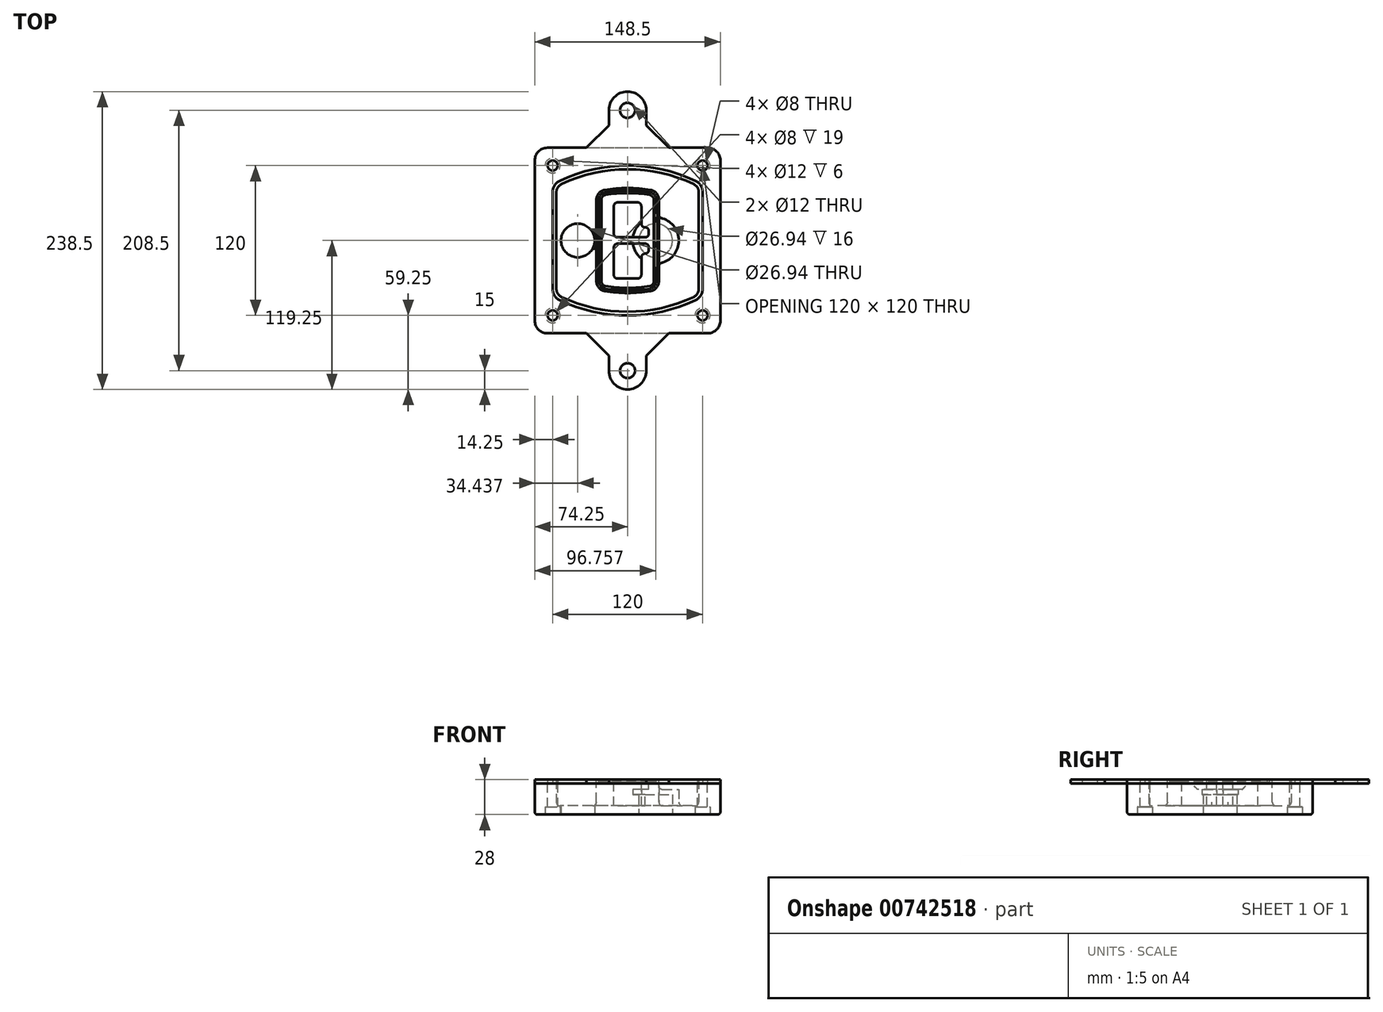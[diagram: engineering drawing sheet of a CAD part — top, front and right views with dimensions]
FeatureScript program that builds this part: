
annotation { "Feature Type Name" : "Feature", "Feature Type Description" : "" }
export const myFeature = defineFeature(function(context is Context, id is Id, definition is map)
    precondition{}
    {
        {
            var Q0;
            Q0=qCreatedBy(makeId("Top.planeOp"),FACE);
            var sketch = newSketch(context, id + "F0", { "sketchPlane" : qUnion([Q0])});
            skPoint(sketch, "E0.rect.middle", {"position": v(0, 0) * mm});
            skLineSegment(sketch, "E1.bottom", {"start": v(-64.25, -74.25) * mm, "end": v(64.25, -74.25) * mm});
            skLineSegment(sketch, "E1.top", {"start": v(-64.25, 74.25) * mm, "end": v(64.25, 74.25) * mm});
            skLineSegment(sketch, "E1.left", {"start": v(-74.25, -64.25) * mm, "end": v(-74.25, 64.25) * mm});
            skLineSegment(sketch, "E1.right", {"start": v(74.25, -64.25) * mm, "end": v(74.25, 64.25) * mm});
            skLineSegment(sketch, "E2", {"start": v(-74.25, 74.25) * mm, "end": v(74.25, -74.25) * mm, "construction": true});
            skLineSegment(sketch, "E3", {"start": v(74.25, 74.25) * mm, "end": v(-74.25, -74.25) * mm, "construction": true});
            skCircle(sketch, "E4", {"center": v(-60, 60) * mm, "radius": 4 * mm});
            skCircle(sketch, "E5", {"center": v(60, 60) * mm, "radius": 4 * mm});
            skCircle(sketch, "E6", {"center": v(60, -60) * mm, "radius": 4 * mm});
            skCircle(sketch, "E7", {"center": v(-60, -60) * mm, "radius": 4 * mm});
            skLineSegment(sketch, "E8", {"start": v(-60, 60) * mm, "end": v(60, 60) * mm, "construction": true});
            skLineSegment(sketch, "E9", {"start": v(60, 60) * mm, "end": v(60, -60) * mm, "construction": true});
            skLineSegment(sketch, "E10", {"start": v(60, -60) * mm, "end": v(-60, -60) * mm, "construction": true});
            skLineSegment(sketch, "E11", {"start": v(-60, -60) * mm, "end": v(-60, 60) * mm, "construction": true});
            skLineSegment(sketch, "E12", {"start": v(-60, 38.83) * mm, "end": v(-60, -38.83) * mm});
            skLineSegment(sketch, "E13", {"start": v(60, 38.83) * mm, "end": v(60, -38.83) * mm});
            skArc(sketch, "E14", {"start": v(54.26, 47.88) * mm, "mid": v(0, 60) * mm, "end": v(-54.26, 47.88) * mm});
            skArc(sketch, "E15", {"start": v(-54.26, -47.88) * mm, "mid": v(0, -60) * mm, "end": v(54.26, -47.88) * mm});
            skLineSegment(sketch, "E16", {"start": v(-60, 0) * mm, "end": v(60, 0) * mm, "construction": true});
            skPoint(sketch, "E17.visualSharp", {"position": v(-60, -45) * mm});
            skArc(sketch, "E17.filletArc", {"start": v(-60, -38.83) * mm, "mid": v(-58.44, -44.2) * mm, "end": v(-54.26, -47.88) * mm});
            skPoint(sketch, "E18.visualSharp", {"position": v(-60, 45) * mm});
            skArc(sketch, "E18.filletArc", {"start": v(-54.26, 47.88) * mm, "mid": v(-58.44, 44.2) * mm, "end": v(-60, 38.83) * mm});
            skPoint(sketch, "E19.visualSharp", {"position": v(60, 45) * mm});
            skArc(sketch, "E19.filletArc", {"start": v(60, 38.83) * mm, "mid": v(58.44, 44.2) * mm, "end": v(54.26, 47.88) * mm});
            skPoint(sketch, "E20.visualSharp", {"position": v(60, -45) * mm});
            skArc(sketch, "E20.filletArc", {"start": v(54.26, -47.88) * mm, "mid": v(58.44, -44.2) * mm, "end": v(60, -38.83) * mm});
            skPoint(sketch, "E21.visualSharp", {"position": v(-74.25, 74.25) * mm});
            skArc(sketch, "E21.filletArc", {"start": v(-64.25, 74.25) * mm, "mid": v(-71.32, 71.32) * mm, "end": v(-74.25, 64.25) * mm});
            skPoint(sketch, "E22.visualSharp", {"position": v(74.25, 74.25) * mm});
            skArc(sketch, "E22.filletArc", {"start": v(74.25, 64.25) * mm, "mid": v(71.32, 71.32) * mm, "end": v(64.25, 74.25) * mm});
            skPoint(sketch, "E23.visualSharp", {"position": v(74.25, -74.25) * mm});
            skArc(sketch, "E23.filletArc", {"start": v(64.25, -74.25) * mm, "mid": v(71.32, -71.32) * mm, "end": v(74.25, -64.25) * mm});
            skPoint(sketch, "E24.visualSharp", {"position": v(-74.25, -74.25) * mm});
            skArc(sketch, "E24.filletArc", {"start": v(-74.25, -64.25) * mm, "mid": v(-71.32, -71.32) * mm, "end": v(-64.25, -74.25) * mm});
            skArc(sketch, "E25.0", {"start": v(57, 38.83) * mm, "mid": v(55.9, 42.58) * mm, "end": v(52.98, 45.17) * mm});
            skLineSegment(sketch, "E25.1", {"start": v(57, 38.83) * mm, "end": v(57, -38.83) * mm});
            skArc(sketch, "E25.2", {"start": v(52.98, -45.17) * mm, "mid": v(55.9, -42.58) * mm, "end": v(57, -38.83) * mm});
            skArc(sketch, "E25.3", {"start": v(-52.98, -45.17) * mm, "mid": v(0, -57) * mm, "end": v(52.98, -45.17) * mm});
            skArc(sketch, "E25.4", {"start": v(-57, -38.83) * mm, "mid": v(-55.9, -42.58) * mm, "end": v(-52.98, -45.17) * mm});
            skArc(sketch, "E25.5", {"start": v(52.98, 45.17) * mm, "mid": v(0, 57) * mm, "end": v(-52.98, 45.17) * mm});
            skLineSegment(sketch, "E25.6", {"start": v(-57, 38.83) * mm, "end": v(-57, -38.83) * mm});
            skArc(sketch, "E25.7", {"start": v(-52.98, 45.17) * mm, "mid": v(-55.9, 42.58) * mm, "end": v(-57, 38.83) * mm});
            skArc(sketch, "E26.0", {"start": v(-55.96, 51.5) * mm, "mid": v(-61.82, 46.33) * mm, "end": v(-64, 38.83) * mm});
            skArc(sketch, "E26.1", {"start": v(55.96, 51.5) * mm, "mid": v(0, 64) * mm, "end": v(-55.96, 51.5) * mm});
            skArc(sketch, "E26.2", {"start": v(64, 38.83) * mm, "mid": v(61.82, 46.33) * mm, "end": v(55.96, 51.5) * mm});
            skLineSegment(sketch, "E26.3", {"start": v(64, 38.83) * mm, "end": v(64, -38.83) * mm});
            skArc(sketch, "E26.4", {"start": v(55.96, -51.5) * mm, "mid": v(61.82, -46.33) * mm, "end": v(64, -38.83) * mm});
            skLineSegment(sketch, "E26.5", {"start": v(-64, 38.83) * mm, "end": v(-64, -38.83) * mm});
            skArc(sketch, "E26.6", {"start": v(-55.96, -51.5) * mm, "mid": v(0, -64) * mm, "end": v(55.96, -51.5) * mm});
            skArc(sketch, "E26.7", {"start": v(-64, -38.83) * mm, "mid": v(-61.82, -46.33) * mm, "end": v(-55.96, -51.5) * mm});
            skSolve(sketch);
        }
        {
            var Q0;
            Q0=makeQuery(id+"F0.imprint","IMPRINT",FACE,{"disambiguationData":[TD([[makeQuery(id+"F0.imprint","IMPRINT",EDGE,{"derivedFrom":sQuery(id+"F0.wireOp",EDGE,"E1.bottom")}),1.0]])]});
            var Q1;
            Q1=makeQuery(id+"F0.imprint","IMPRINT",FACE,{"disambiguationData":[TD([[makeQuery(id+"F0.imprint","IMPRINT",EDGE,{"derivedFrom":sQuery(id+"F0.wireOp",EDGE,"E12")}),1.0]])]});
            var Q2;
            Q2=makeQuery(id+"F0.imprint","IMPRINT",FACE,{"disambiguationData":[TD([[makeQuery(id+"F0.imprint","IMPRINT",EDGE,{"derivedFrom":sQuery(id+"F0.wireOp",EDGE,"E25.0")}),1.0]])]});
            var Q3;
            Q3=makeQuery(id+"F0.imprint","IMPRINT",FACE,{"disambiguationData":[TD([[makeQuery(id+"F0.imprint","IMPRINT",EDGE,{"derivedFrom":sQuery(id+"F0.wireOp",EDGE,"E12")}),-1.0]])]});
            extrude(context, id + "F1", {"entities" : qUnion([Q0, Q1, Q2, Q3]), "oppositeDirection" : true, "depth" : 25 * mm});
        }
        {
            var Q0;
            Q0=makeQuery(id+"F0.imprint","IMPRINT",FACE,{"disambiguationData":[TD([[makeQuery(id+"F0.imprint","IMPRINT",EDGE,{"derivedFrom":sQuery(id+"F0.wireOp",EDGE,"E12")}),1.0]])]});
            extrude(context, id + "F2", {"entities" : qUnion([Q0]), "operationType" : NewBodyOperationType.ADD, "depth" : 3 * mm});
        }
        {
            var Q0;
            Q0=makeQuery(id+"F0.imprint","IMPRINT",FACE,{"disambiguationData":[TD([[makeQuery(id+"F0.imprint","IMPRINT",EDGE,{"derivedFrom":sQuery(id+"F0.wireOp",EDGE,"E25.0")}),1.0]])]});
            extrude(context, id + "F3", {"entities" : qUnion([Q0]), "operationType" : NewBodyOperationType.REMOVE, "oppositeDirection" : true, "depth" : 18 * mm});
        }
        {
            var Q0;
            Q0=makeQuery(id+"F2.opExtrude","CAP_FACE",FACE,{"disambiguationData":[OSD([sQuery(id+"F0.wireOp",EDGE,"E12"),sQuery(id+"F0.wireOp",EDGE,"E13"),sQuery(id+"F0.wireOp",EDGE,"E14"),sQuery(id+"F0.wireOp",EDGE,"E15"),sQuery(id+"F0.wireOp",EDGE,"E17.filletArc"),sQuery(id+"F0.wireOp",EDGE,"E18.filletArc"),sQuery(id+"F0.wireOp",EDGE,"E19.filletArc"),sQuery(id+"F0.wireOp",EDGE,"E20.filletArc"),sQuery(id+"F0.wireOp",EDGE,"E25.0"),sQuery(id+"F0.wireOp",EDGE,"E25.1"),sQuery(id+"F0.wireOp",EDGE,"E25.2"),sQuery(id+"F0.wireOp",EDGE,"E25.3"),sQuery(id+"F0.wireOp",EDGE,"E25.4"),sQuery(id+"F0.wireOp",EDGE,"E25.5"),sQuery(id+"F0.wireOp",EDGE,"E25.6"),sQuery(id+"F0.wireOp",EDGE,"E25.7")])],"isStart":false});
            var sketch = newSketch(context, id + "F4", { "sketchPlane" : qUnion([Q0])});
            skArc(sketch, "E27.0", {"start": v(-18.34, -40.45) * mm, "mid": v(0, -42) * mm, "end": v(18.34, -40.45) * mm});
            skArc(sketch, "E28.0", {"start": v(18.34, 40.45) * mm, "mid": v(0, 42) * mm, "end": v(-18.34, 40.45) * mm});
            skLineSegment(sketch, "E29", {"start": v(-25, 32.57) * mm, "end": v(-25, -32.57) * mm});
            skLineSegment(sketch, "E30", {"start": v(25, 32.57) * mm, "end": v(25, -32.57) * mm});
            skLineSegment(sketch, "E31", {"start": v(-25, 39.1) * mm, "end": v(25, 39.1) * mm, "construction": true});
            skLineSegment(sketch, "E32", {"start": v(-25, -39.1) * mm, "end": v(25, -39.1) * mm, "construction": true});
            skPoint(sketch, "E33.visualSharp", {"position": v(-25, 39.1) * mm});
            skArc(sketch, "E33.filletArc", {"start": v(-18.34, 40.45) * mm, "mid": v(-23.11, 37.73) * mm, "end": v(-25, 32.57) * mm});
            skPoint(sketch, "E34.visualSharp", {"position": v(25, 39.1) * mm});
            skArc(sketch, "E34.filletArc", {"start": v(25, 32.57) * mm, "mid": v(23.11, 37.73) * mm, "end": v(18.34, 40.45) * mm});
            skPoint(sketch, "E35.visualSharp", {"position": v(25, -39.1) * mm});
            skArc(sketch, "E35.filletArc", {"start": v(18.34, -40.45) * mm, "mid": v(23.11, -37.73) * mm, "end": v(25, -32.57) * mm});
            skPoint(sketch, "E36.visualSharp", {"position": v(-25, -39.1) * mm});
            skArc(sketch, "E36.filletArc", {"start": v(-25, -32.57) * mm, "mid": v(-23.11, -37.73) * mm, "end": v(-18.34, -40.45) * mm});
            skArc(sketch, "E37.0", {"start": v(52.98, 45.17) * mm, "mid": v(0, 57) * mm, "end": v(-52.98, 45.17) * mm});
            skArc(sketch, "E37.1", {"start": v(-52.98, 45.17) * mm, "mid": v(-55.9, 42.58) * mm, "end": v(-57, 38.83) * mm});
            skLineSegment(sketch, "E37.2", {"start": v(-57, 38.83) * mm, "end": v(-57, -38.83) * mm});
            skArc(sketch, "E37.3", {"start": v(-57, -38.83) * mm, "mid": v(-55.9, -42.58) * mm, "end": v(-52.98, -45.17) * mm});
            skArc(sketch, "E37.4", {"start": v(-52.98, -45.17) * mm, "mid": v(0, -57) * mm, "end": v(52.98, -45.17) * mm});
            skArc(sketch, "E37.5", {"start": v(52.98, -45.17) * mm, "mid": v(55.9, -42.58) * mm, "end": v(57, -38.83) * mm});
            skLineSegment(sketch, "E37.6", {"start": v(57, 38.83) * mm, "end": v(57, -38.83) * mm});
            skArc(sketch, "E37.7", {"start": v(57, 38.83) * mm, "mid": v(55.9, 42.58) * mm, "end": v(52.98, 45.17) * mm});
            skLineSegment(sketch, "E38.0", {"start": v(23, 32.57) * mm, "end": v(23, -32.57) * mm});
            skArc(sketch, "E38.1", {"start": v(18, -38.48) * mm, "mid": v(21.58, -36.44) * mm, "end": v(23, -32.57) * mm});
            skArc(sketch, "E38.2", {"start": v(-18, -38.48) * mm, "mid": v(0, -40) * mm, "end": v(18, -38.48) * mm});
            skArc(sketch, "E38.3", {"start": v(-23, -32.57) * mm, "mid": v(-21.58, -36.44) * mm, "end": v(-18, -38.48) * mm});
            skLineSegment(sketch, "E38.4", {"start": v(-23, 32.57) * mm, "end": v(-23, -32.57) * mm});
            skArc(sketch, "E38.5", {"start": v(23, 32.57) * mm, "mid": v(21.58, 36.44) * mm, "end": v(18, 38.48) * mm});
            skArc(sketch, "E38.6", {"start": v(-18, 38.48) * mm, "mid": v(-21.58, 36.44) * mm, "end": v(-23, 32.57) * mm});
            skArc(sketch, "E38.7", {"start": v(18, 38.48) * mm, "mid": v(0, 40) * mm, "end": v(-18, 38.48) * mm});
            skArc(sketch, "E39.0", {"start": v(21, 32.57) * mm, "mid": v(20.06, 35.15) * mm, "end": v(17.67, 36.5) * mm});
            skLineSegment(sketch, "E39.1", {"start": v(21, 32.57) * mm, "end": v(21, -32.57) * mm});
            skArc(sketch, "E39.2", {"start": v(17.67, -36.5) * mm, "mid": v(20.06, -35.15) * mm, "end": v(21, -32.57) * mm});
            skArc(sketch, "E39.3", {"start": v(-17.67, -36.5) * mm, "mid": v(0, -38) * mm, "end": v(17.67, -36.5) * mm});
            skArc(sketch, "E39.4", {"start": v(-21, -32.57) * mm, "mid": v(-20.06, -35.15) * mm, "end": v(-17.67, -36.5) * mm});
            skArc(sketch, "E39.5", {"start": v(17.67, 36.5) * mm, "mid": v(0, 38) * mm, "end": v(-17.67, 36.5) * mm});
            skLineSegment(sketch, "E39.6", {"start": v(-21, 32.57) * mm, "end": v(-21, -32.57) * mm});
            skArc(sketch, "E39.7", {"start": v(-17.67, 36.5) * mm, "mid": v(-20.06, 35.15) * mm, "end": v(-21, 32.57) * mm});
            skLineSegment(sketch, "E40", {"start": v(-25, 0) * mm, "end": v(25, 0) * mm, "construction": true});
            skLineSegment(sketch, "E41", {"start": v(-11, 5.5) * mm, "end": v(-11, 27.5) * mm});
            skLineSegment(sketch, "E42", {"start": v(-8, 30.5) * mm, "end": v(8, 30.5) * mm});
            skLineSegment(sketch, "E43", {"start": v(11, 27.5) * mm, "end": v(11, 13.5) * mm});
            skLineSegment(sketch, "E44", {"start": v(14, 10.5) * mm, "end": v(14, 10.5) * mm});
            skLineSegment(sketch, "E45", {"start": v(17, 7.5) * mm, "end": v(17, 5.5) * mm});
            skLineSegment(sketch, "E46", {"start": v(14, 2.5) * mm, "end": v(-8, 2.5) * mm});
            skPoint(sketch, "E47.visualSharp", {"position": v(-11, 30.5) * mm});
            skArc(sketch, "E47.filletArc", {"start": v(-8, 30.5) * mm, "mid": v(-10.12, 29.62) * mm, "end": v(-11, 27.5) * mm});
            skPoint(sketch, "E48.visualSharp", {"position": v(11, 30.5) * mm});
            skArc(sketch, "E48.filletArc", {"start": v(11, 27.5) * mm, "mid": v(10.12, 29.62) * mm, "end": v(8, 30.5) * mm});
            skPoint(sketch, "E49.visualSharp", {"position": v(11, 10.5) * mm});
            skArc(sketch, "E49.filletArc", {"start": v(11, 13.5) * mm, "mid": v(11.88, 11.38) * mm, "end": v(14, 10.5) * mm});
            skPoint(sketch, "E50.visualSharp", {"position": v(17, 10.5) * mm});
            skArc(sketch, "E50.filletArc", {"start": v(17, 7.5) * mm, "mid": v(16.12, 9.62) * mm, "end": v(14, 10.5) * mm});
            skPoint(sketch, "E51.visualSharp", {"position": v(17, 2.5) * mm});
            skArc(sketch, "E51.filletArc", {"start": v(14, 2.5) * mm, "mid": v(16.12, 3.38) * mm, "end": v(17, 5.5) * mm});
            skPoint(sketch, "E52.visualSharp", {"position": v(-11, 2.5) * mm});
            skArc(sketch, "E52.filletArc", {"start": v(-11, 5.5) * mm, "mid": v(-10.12, 3.38) * mm, "end": v(-8, 2.5) * mm});
            skLineSegment(sketch, "E53.0.MirrorCS", {"start": v(14, -2.5) * mm, "end": v(-8, -2.5) * mm});
            skArc(sketch, "E54.0.MirrorCS", {"start": v(-11, -5.5) * mm, "mid": v(-10.12, -3.38) * mm, "end": v(-8, -2.5) * mm});
            skLineSegment(sketch, "E55.0.MirrorCS", {"start": v(-11, -5.5) * mm, "end": v(-11, -27.5) * mm});
            skArc(sketch, "E56.0.MirrorCS", {"start": v(-8, -30.5) * mm, "mid": v(-10.12, -29.62) * mm, "end": v(-11, -27.5) * mm});
            skLineSegment(sketch, "E57.0.MirrorCS", {"start": v(-8, -30.5) * mm, "end": v(8, -30.5) * mm});
            skArc(sketch, "E58.0.MirrorCS", {"start": v(11, -27.5) * mm, "mid": v(10.12, -29.62) * mm, "end": v(8, -30.5) * mm});
            skLineSegment(sketch, "E59.0.MirrorCS", {"start": v(11, -27.5) * mm, "end": v(11, -13.5) * mm});
            skArc(sketch, "E60.0.MirrorCS", {"start": v(11, -13.5) * mm, "mid": v(11.88, -11.38) * mm, "end": v(14, -10.5) * mm});
            skArc(sketch, "E61.0.MirrorCS", {"start": v(17, -7.5) * mm, "mid": v(16.12, -9.62) * mm, "end": v(14, -10.5) * mm});
            skLineSegment(sketch, "E62.0.MirrorCS", {"start": v(17, -7.5) * mm, "end": v(17, -5.5) * mm});
            skArc(sketch, "E63.0.MirrorCS", {"start": v(14, -2.5) * mm, "mid": v(16.12, -3.38) * mm, "end": v(17, -5.5) * mm});
            skSolve(sketch);
        }
        {
            var Q0;
            Q0=makeQuery(id+"F4.imprint","IMPRINT",FACE,{"disambiguationData":[TD([[makeQuery(id+"F4.imprint","IMPRINT",EDGE,{"derivedFrom":sQuery(id+"F4.wireOp",EDGE,"E27.0")}),1.0]])]});
            var Q1;
            Q1=makeQuery(id+"F4.imprint","IMPRINT",FACE,{"disambiguationData":[TD([[makeQuery(id+"F4.imprint","IMPRINT",EDGE,{"derivedFrom":sQuery(id+"F4.wireOp",EDGE,"E38.0")}),-1.0]])]});
            var Q2;
            Q2=makeQuery(id+"F4.imprint","IMPRINT",FACE,{"disambiguationData":[TD([[makeQuery(id+"F4.imprint","IMPRINT",EDGE,{"derivedFrom":sQuery(id+"F4.wireOp",EDGE,"E39.0")}),1.0]])]});
            extrude(context, id + "F5", {"entities" : qUnion([Q0, Q1, Q2]), "operationType" : NewBodyOperationType.ADD, "endBound" : BoundingType.UP_TO_NEXT, "oppositeDirection" : true, "depth" : 25 * mm});
        }
        {
            var Q0;
            Q0=makeQuery(id+"F4.imprint","IMPRINT",FACE,{"disambiguationData":[TD([[makeQuery(id+"F4.imprint","IMPRINT",EDGE,{"derivedFrom":sQuery(id+"F4.wireOp",EDGE,"E38.0")}),-1.0]])]});
            extrude(context, id + "F6", {"entities" : qUnion([Q0]), "operationType" : NewBodyOperationType.REMOVE, "oppositeDirection" : true, "depth" : 2 * mm});
        }
        {
            var Q0;
            Q0=makeQuery(id+"F1.opExtrude","CAP_FACE",FACE,{"disambiguationData":[OSD([sQuery(id+"F0.wireOp",EDGE,"E1.bottom"),sQuery(id+"F0.wireOp",EDGE,"E1.top"),sQuery(id+"F0.wireOp",EDGE,"E1.left"),sQuery(id+"F0.wireOp",EDGE,"E1.right"),sQuery(id+"F0.wireOp",EDGE,"E4"),sQuery(id+"F0.wireOp",EDGE,"E5"),sQuery(id+"F0.wireOp",EDGE,"E6"),sQuery(id+"F0.wireOp",EDGE,"E7"),sQuery(id+"F0.wireOp",EDGE,"E21.filletArc"),sQuery(id+"F0.wireOp",EDGE,"E22.filletArc"),sQuery(id+"F0.wireOp",EDGE,"E23.filletArc"),sQuery(id+"F0.wireOp",EDGE,"E24.filletArc")])],"isStart":false});
            var sketch = newSketch(context, id + "F7", { "sketchPlane" : qUnion([Q0])});
            skCircle(sketch, "E64", {"center": v(22.5, 0) * mm, "radius": 13.47 * mm});
            skCircle(sketch, "E65", {"center": v(-39.81, 0) * mm, "radius": 13.47 * mm});
            skLineSegment(sketch, "E66", {"start": v(74.25, 0) * mm, "end": v(-74.25, 0) * mm});
            skCircle(sketch, "E67", {"center": v(22.5, 0) * mm, "radius": 18.47 * mm});
            skCircle(sketch, "E68", {"center": v(60, -60) * mm, "radius": 6 * mm});
            skCircle(sketch, "E69", {"center": v(-60, -60) * mm, "radius": 6 * mm});
            skCircle(sketch, "E70", {"center": v(-60, 60) * mm, "radius": 6 * mm});
            skCircle(sketch, "E71", {"center": v(60, 60) * mm, "radius": 6 * mm});
            skSolve(sketch);
        }
        {
            var Q0;
            {var subQ1=sQuery(id+"F7.wireOp",EDGE,"E66");var subQ4=sQuery(id+"F7.wireOp",EDGE,"E64");var subQ6=makeQuery(id+"F7.imprint","INTERSECT",VERTEX,{"disambiguationData":[OD(0.0)],"derivedFrom":[subQ4,subQ1]});Q0=makeQuery(id+"F7.imprint","IMPRINT",FACE,{"disambiguationData":[TD([[makeQuery(id+"F7.imprint","IMPRINT",EDGE,{"disambiguationData":[TD([[subQ6,-1.0]])],"derivedFrom":subQ4}),-1.0]])]});}
            var Q1;
            {var subQ0=sQuery(id+"F7.wireOp",EDGE,"E66");var subQ1=sQuery(id+"F7.wireOp",EDGE,"E64");var subQ3=makeQuery(id+"F7.imprint","INTERSECT",VERTEX,{"disambiguationData":[OD(0.0)],"derivedFrom":[subQ1,subQ0]});Q1=makeQuery(id+"F7.imprint","IMPRINT",FACE,{"disambiguationData":[TD([[makeQuery(id+"F7.imprint","IMPRINT",EDGE,{"disambiguationData":[TD([[subQ3,-1.0]])],"derivedFrom":subQ1}),1.0]])]});}
            var Q2;
            {var subQ0=sQuery(id+"F7.wireOp",EDGE,"E66");var subQ1=sQuery(id+"F7.wireOp",EDGE,"E64");var subQ3=makeQuery(id+"F7.imprint","INTERSECT",VERTEX,{"disambiguationData":[OD(0.0)],"derivedFrom":[subQ1,subQ0]});Q2=makeQuery(id+"F7.imprint","IMPRINT",FACE,{"disambiguationData":[TD([[makeQuery(id+"F7.imprint","IMPRINT",EDGE,{"disambiguationData":[TD([[subQ3,1.0]])],"derivedFrom":subQ1}),1.0]])]});}
            var Q3;
            {var subQ1=sQuery(id+"F7.wireOp",EDGE,"E66");var subQ4=sQuery(id+"F7.wireOp",EDGE,"E64");var subQ6=makeQuery(id+"F7.imprint","INTERSECT",VERTEX,{"disambiguationData":[OD(0.0)],"derivedFrom":[subQ4,subQ1]});Q3=makeQuery(id+"F7.imprint","IMPRINT",FACE,{"disambiguationData":[TD([[makeQuery(id+"F7.imprint","IMPRINT",EDGE,{"disambiguationData":[TD([[subQ6,1.0]])],"derivedFrom":subQ4}),-1.0]])]});}
            extrude(context, id + "F8", {"entities" : qUnion([Q0, Q1, Q2, Q3]), "operationType" : NewBodyOperationType.ADD, "oppositeDirection" : true, "depth" : 20 * mm});
        }
        {
            var Q0;
            {var subQ0=sQuery(id+"F7.wireOp",EDGE,"E66");var subQ1=sQuery(id+"F7.wireOp",EDGE,"E64");var subQ3=makeQuery(id+"F7.imprint","INTERSECT",VERTEX,{"disambiguationData":[OD(0.0)],"derivedFrom":[subQ1,subQ0]});Q0=makeQuery(id+"F7.imprint","IMPRINT",FACE,{"disambiguationData":[TD([[makeQuery(id+"F7.imprint","IMPRINT",EDGE,{"disambiguationData":[TD([[subQ3,-1.0]])],"derivedFrom":subQ1}),1.0]])]});}
            var Q1;
            {var subQ0=sQuery(id+"F7.wireOp",EDGE,"E66");var subQ1=sQuery(id+"F7.wireOp",EDGE,"E64");var subQ3=makeQuery(id+"F7.imprint","INTERSECT",VERTEX,{"disambiguationData":[OD(0.0)],"derivedFrom":[subQ1,subQ0]});Q1=makeQuery(id+"F7.imprint","IMPRINT",FACE,{"disambiguationData":[TD([[makeQuery(id+"F7.imprint","IMPRINT",EDGE,{"disambiguationData":[TD([[subQ3,1.0]])],"derivedFrom":subQ1}),1.0]])]});}
            extrude(context, id + "F9", {"entities" : qUnion([Q0, Q1]), "operationType" : NewBodyOperationType.REMOVE, "oppositeDirection" : true, "depth" : 16 * mm});
        }
        {
            var Q0;
            {var subQ0=sQuery(id+"F7.wireOp",EDGE,"E66");var subQ1=sQuery(id+"F7.wireOp",EDGE,"E65");var subQ3=makeQuery(id+"F7.imprint","INTERSECT",VERTEX,{"disambiguationData":[OD(0.0)],"derivedFrom":[subQ1,subQ0]});Q0=makeQuery(id+"F7.imprint","IMPRINT",FACE,{"disambiguationData":[TD([[makeQuery(id+"F7.imprint","IMPRINT",EDGE,{"disambiguationData":[TD([[subQ3,-1.0]])],"derivedFrom":subQ1}),1.0]])]});}
            var Q1;
            {var subQ0=sQuery(id+"F7.wireOp",EDGE,"E66");var subQ1=sQuery(id+"F7.wireOp",EDGE,"E65");var subQ3=makeQuery(id+"F7.imprint","INTERSECT",VERTEX,{"disambiguationData":[OD(0.0)],"derivedFrom":[subQ1,subQ0]});Q1=makeQuery(id+"F7.imprint","IMPRINT",FACE,{"disambiguationData":[TD([[makeQuery(id+"F7.imprint","IMPRINT",EDGE,{"disambiguationData":[TD([[subQ3,1.0]])],"derivedFrom":subQ1}),1.0]])]});}
            extrude(context, id + "F10", {"entities" : qUnion([Q0, Q1]), "operationType" : NewBodyOperationType.REMOVE, "oppositeDirection" : true, "depth" : 25 * mm});
        }
        {
            var Q0;
            Q0=makeQuery(id+"F7.imprint","IMPRINT",FACE,{"disambiguationData":[TD([[makeQuery(id+"F7.imprint","IMPRINT",EDGE,{"derivedFrom":sQuery(id+"F7.wireOp",EDGE,"E68")}),1.0]])]});
            var Q1;
            Q1=makeQuery(id+"F7.imprint","IMPRINT",FACE,{"disambiguationData":[TD([[makeQuery(id+"F7.imprint","IMPRINT",EDGE,{"derivedFrom":makeQuery(id+"F1.opExtrude","CAP_EDGE",EDGE,{"disambiguationData":[OSD([sQuery(id+"F0.wireOp",EDGE,"E5")])],"isStart":false})}),-1.0]])]});
            var Q2;
            Q2=makeQuery(id+"F7.imprint","IMPRINT",FACE,{"disambiguationData":[TD([[makeQuery(id+"F7.imprint","IMPRINT",EDGE,{"derivedFrom":sQuery(id+"F7.wireOp",EDGE,"E69")}),1.0]])]});
            var Q3;
            Q3=makeQuery(id+"F7.imprint","IMPRINT",FACE,{"disambiguationData":[TD([[makeQuery(id+"F7.imprint","IMPRINT",EDGE,{"derivedFrom":makeQuery(id+"F1.opExtrude","CAP_EDGE",EDGE,{"disambiguationData":[OSD([sQuery(id+"F0.wireOp",EDGE,"E4")])],"isStart":false})}),-1.0]])]});
            var Q4;
            Q4=makeQuery(id+"F7.imprint","IMPRINT",FACE,{"disambiguationData":[TD([[makeQuery(id+"F7.imprint","IMPRINT",EDGE,{"derivedFrom":sQuery(id+"F7.wireOp",EDGE,"E70")}),1.0]])]});
            var Q5;
            Q5=makeQuery(id+"F7.imprint","IMPRINT",FACE,{"disambiguationData":[TD([[makeQuery(id+"F7.imprint","IMPRINT",EDGE,{"derivedFrom":makeQuery(id+"F1.opExtrude","CAP_EDGE",EDGE,{"disambiguationData":[OSD([sQuery(id+"F0.wireOp",EDGE,"E7")])],"isStart":false})}),-1.0]])]});
            var Q6;
            Q6=makeQuery(id+"F7.imprint","IMPRINT",FACE,{"disambiguationData":[TD([[makeQuery(id+"F7.imprint","IMPRINT",EDGE,{"derivedFrom":sQuery(id+"F7.wireOp",EDGE,"E71")}),1.0]])]});
            var Q7;
            Q7=makeQuery(id+"F7.imprint","IMPRINT",FACE,{"disambiguationData":[TD([[makeQuery(id+"F7.imprint","IMPRINT",EDGE,{"derivedFrom":makeQuery(id+"F1.opExtrude","CAP_EDGE",EDGE,{"disambiguationData":[OSD([sQuery(id+"F0.wireOp",EDGE,"E6")])],"isStart":false})}),-1.0]])]});
            extrude(context, id + "F11", {"entities" : qUnion([Q0, Q1, Q2, Q3, Q4, Q5, Q6, Q7]), "operationType" : NewBodyOperationType.REMOVE, "oppositeDirection" : true, "depth" : 6 * mm});
        }
        {
            var Q0;
            Q0=makeQuery(id+"F9.boolean.opBoolean","COPY",FACE,{"derivedFrom":makeQuery(id+"F9.opExtrude","CAP_FACE",FACE,{"disambiguationData":[OSD([sQuery(id+"F7.wireOp",EDGE,"E64")])],"isStart":false})});
            var sketch = newSketch(context, id + "F12", { "sketchPlane" : qUnion([Q0])});
            skArc(sketch, "E72.0", {"start": v(11, 14.45) * mm, "mid": v(6.45, 9.13) * mm, "end": v(4.2, 2.5) * mm});
            skArc(sketch, "E72.1", {"start": v(4.2, -2.5) * mm, "mid": v(6.45, -9.13) * mm, "end": v(11, -14.45) * mm});
            skLineSegment(sketch, "E73", {"start": v(4.2, -2.5) * mm, "end": v(14, -2.5) * mm});
            skLineSegment(sketch, "E74.0", {"start": v(14, 2.5) * mm, "end": v(4.2, 2.5) * mm});
            skArc(sketch, "E74.1", {"start": v(14, 2.5) * mm, "mid": v(16.12, 3.38) * mm, "end": v(17, 5.5) * mm});
            skLineSegment(sketch, "E74.2", {"start": v(17, 7.5) * mm, "end": v(17, 5.5) * mm});
            skArc(sketch, "E74.3", {"start": v(17, 7.5) * mm, "mid": v(16.12, 9.62) * mm, "end": v(14, 10.5) * mm});
            skArc(sketch, "E74.4", {"start": v(11, 13.5) * mm, "mid": v(11.88, 11.38) * mm, "end": v(14, 10.5) * mm});
            skLineSegment(sketch, "E74.5", {"start": v(11, 14.45) * mm, "end": v(11, 13.5) * mm});
            skLineSegment(sketch, "E74.7", {"start": v(14, -2.5) * mm, "end": v(4.2, -2.5) * mm});
            skArc(sketch, "E74.8", {"start": v(14, -2.5) * mm, "mid": v(16.12, -3.38) * mm, "end": v(17, -5.5) * mm});
            skLineSegment(sketch, "E74.9", {"start": v(17, -7.5) * mm, "end": v(17, -5.5) * mm});
            skArc(sketch, "E74.10", {"start": v(17, -7.5) * mm, "mid": v(16.12, -9.62) * mm, "end": v(14, -10.5) * mm});
            skArc(sketch, "E74.11", {"start": v(11, -13.5) * mm, "mid": v(11.88, -11.38) * mm, "end": v(14, -10.5) * mm});
            skLineSegment(sketch, "E74.12", {"start": v(11, -14.45) * mm, "end": v(11, -13.5) * mm});
            skPoint(sketch, "E75.orphan", {"position": v(11, -27.5) * mm});
            skPoint(sketch, "E76.orphan", {"position": v(-8, -2.5) * mm});
            skPoint(sketch, "E77.orphan", {"position": v(-8, 2.5) * mm});
            skPoint(sketch, "E78.orphan", {"position": v(11, 27.5) * mm});
            skSolve(sketch);
        }
        {
            var Q0;
            {var subQ7=sQuery(id+"F12.wireOp",EDGE,"E72.0");var subQ14=sQuery(id+"F12.wireOp",EDGE,"E72.1");var subQ16=sQuery(id+"F12.wireOp",EDGE,"E74.1");var subQ18=sQuery(id+"F12.wireOp",EDGE,"E74.8");Q0=qUnion([makeQuery(id+"F12.imprint","IMPRINT",FACE,{"disambiguationData":[TD([[makeQuery(id+"F12.imprint","IMPRINT",EDGE,{"derivedFrom":subQ7}),1.0]])]}),makeQuery(id+"F12.imprint","IMPRINT",FACE,{"disambiguationData":[TD([[makeQuery(id+"F12.imprint","IMPRINT",EDGE,{"derivedFrom":subQ14}),1.0]])]}),makeQuery(id+"F12.imprint","IMPRINT",FACE,{"disambiguationData":[TD([[makeQuery(id+"F12.imprint","IMPRINT",EDGE,{"derivedFrom":subQ16}),1.0]])]}),makeQuery(id+"F12.imprint","IMPRINT",FACE,{"disambiguationData":[TD([[makeQuery(id+"F12.imprint","IMPRINT",EDGE,{"derivedFrom":subQ18}),-1.0]])]})]);}
            var Q1;
            Q1=makeQuery(id+"F5.boolean.opBoolean","SPLIT",FACE,{"disambiguationData":[TD([makeQuery(id+"F5.opExtrude","SWEPT_FACE",FACE,{"disambiguationData":[OSD([sQuery(id+"F4.wireOp",EDGE,"E41")])]})])],"derivedFrom":makeQuery(id+"F3.boolean.opBoolean","COPY",FACE,{"derivedFrom":makeQuery(id+"F3.opExtrude","CAP_FACE",FACE,{"disambiguationData":[OSD([sQuery(id+"F0.wireOp",EDGE,"E25.0"),sQuery(id+"F0.wireOp",EDGE,"E25.1"),sQuery(id+"F0.wireOp",EDGE,"E25.2"),sQuery(id+"F0.wireOp",EDGE,"E25.3"),sQuery(id+"F0.wireOp",EDGE,"E25.4"),sQuery(id+"F0.wireOp",EDGE,"E25.5"),sQuery(id+"F0.wireOp",EDGE,"E25.6"),sQuery(id+"F0.wireOp",EDGE,"E25.7")])],"isStart":false})})});
            extrude(context, id + "F13", {"entities" : qUnion([Q0]), "operationType" : NewBodyOperationType.REMOVE, "endBound" : BoundingType.UP_TO_SURFACE, "endBoundEntityFace" : qUnion([Q1]), "depth" : 25 * mm});
        }
        {
            var Q0;
            Q0=makeQuery(id+"F3.boolean.opBoolean","COPY",EDGE,{"derivedFrom":makeQuery(id+"F3.opExtrude","CAP_EDGE",EDGE,{"disambiguationData":[OSD([sQuery(id+"F0.wireOp",EDGE,"E25.6")])],"isStart":false})});
            var Q1;
            Q1=makeQuery(id+"F8.boolean.opBoolean","INTERSECT",EDGE,{"derivedFrom":[makeQuery(id+"F5.opExtrude","SWEPT_FACE",FACE,{"disambiguationData":[OSD([sQuery(id+"F4.wireOp",EDGE,"E30")])]}),makeQuery(id+"F8.opExtrude","CAP_FACE",FACE,{"disambiguationData":[OSD([sQuery(id+"F7.wireOp",EDGE,"E67")])],"isStart":false})]});
            var Q2;
            Q2=makeQuery(id+"F8.boolean.opBoolean","INTERSECT",EDGE,{"disambiguationData":[OD(1.0)],"derivedFrom":[makeQuery(id+"F5.opExtrude","SWEPT_FACE",FACE,{"disambiguationData":[OSD([sQuery(id+"F4.wireOp",EDGE,"E30")])]}),makeQuery(id+"F8.opExtrude","SWEPT_FACE",FACE,{"disambiguationData":[OSD([sQuery(id+"F7.wireOp",EDGE,"E67")])]})]});
            var Q3;
            {var subQ0=sQuery(id+"F4.wireOp",EDGE,"E30");Q3=makeQuery(id+"F8.boolean.opBoolean","SPLIT",EDGE,{"disambiguationData":[TD([makeQuery(id+"F5.opExtrude","SWEPT_FACE",FACE,{"disambiguationData":[OSD([sQuery(id+"F4.wireOp",EDGE,"E35.filletArc")])]})])],"derivedFrom":makeQuery(id+"F5.opExtrude","CAP_EDGE",EDGE,{"disambiguationData":[OSD([subQ0])],"isStart":false})});}
            var Q4;
            {var subQ0=sQuery(id+"F0.wireOp",EDGE,"E25.7");var subQ1=sQuery(id+"F0.wireOp",EDGE,"E25.1");var subQ2=sQuery(id+"F0.wireOp",EDGE,"E25.6");var subQ3=sQuery(id+"F0.wireOp",EDGE,"E25.5");var subQ4=sQuery(id+"F0.wireOp",EDGE,"E25.4");var subQ5=sQuery(id+"F0.wireOp",EDGE,"E25.0");var subQ6=sQuery(id+"F0.wireOp",EDGE,"E25.2");var subQ7=sQuery(id+"F0.wireOp",EDGE,"E25.3");Q4=makeQuery(id+"F8.boolean.opBoolean","INTERSECT",EDGE,{"derivedFrom":[makeQuery(id+"F5.boolean.opBoolean","SPLIT",FACE,{"disambiguationData":[TD([makeQuery(id+"F2.opExtrude","SWEPT_FACE",FACE,{"disambiguationData":[OSD([subQ5])]})])],"derivedFrom":makeQuery(id+"F3.boolean.opBoolean","COPY",FACE,{"derivedFrom":makeQuery(id+"F3.opExtrude","CAP_FACE",FACE,{"disambiguationData":[OSD([subQ5,subQ1,subQ6,subQ7,subQ4,subQ3,subQ2,subQ0])],"isStart":false})})}),makeQuery(id+"F8.opExtrude","SWEPT_FACE",FACE,{"disambiguationData":[OSD([sQuery(id+"F7.wireOp",EDGE,"E67")])]})]});}
            var Q5;
            Q5=makeQuery(id+"F8.boolean.opBoolean","INTERSECT",EDGE,{"disambiguationData":[OD(0.0)],"derivedFrom":[makeQuery(id+"F5.opExtrude","SWEPT_FACE",FACE,{"disambiguationData":[OSD([sQuery(id+"F4.wireOp",EDGE,"E30")])]}),makeQuery(id+"F8.opExtrude","SWEPT_FACE",FACE,{"disambiguationData":[OSD([sQuery(id+"F7.wireOp",EDGE,"E67")])]})]});
            fillet(context, id + "F14", {"entities" : qUnion([Q0, Q1, Q2, Q3, Q4, Q5]), "radius" : 3 * mm, "tangentPropagation" : true, "allowEdgeOverflow" : false});
        }
        {
            var Q0;
            Q0=makeQuery(id+"F1.opExtrude","CAP_EDGE",EDGE,{"disambiguationData":[OSD([sQuery(id+"F0.wireOp",EDGE,"E1.bottom")])],"isStart":false});
            fillet(context, id + "F15", {"entities" : qUnion([Q0]), "radius" : 2 * mm, "tangentPropagation" : true, "allowEdgeOverflow" : false});
        }
        {
            var Q0;
            {var subQ0=sQuery(id+"F0.wireOp",EDGE,"E21.filletArc");var subQ1=sQuery(id+"F0.wireOp",EDGE,"E7");var subQ2=sQuery(id+"F0.wireOp",EDGE,"E6");var subQ3=sQuery(id+"F0.wireOp",EDGE,"E5");var subQ4=sQuery(id+"F0.wireOp",EDGE,"E4");var subQ5=sQuery(id+"F0.wireOp",EDGE,"E22.filletArc");var subQ6=sQuery(id+"F0.wireOp",EDGE,"E1.bottom");var subQ7=sQuery(id+"F0.wireOp",EDGE,"E1.right");var subQ8=sQuery(id+"F0.wireOp",EDGE,"E1.top");var subQ9=sQuery(id+"F0.wireOp",EDGE,"E1.left");var subQ10=sQuery(id+"F0.wireOp",EDGE,"E23.filletArc");var subQ11=sQuery(id+"F0.wireOp",EDGE,"E24.filletArc");Q0=makeQuery(id+"F2.boolean.opBoolean","SPLIT",FACE,{"disambiguationData":[TD([makeQuery(id+"F1.opExtrude","SWEPT_FACE",FACE,{"disambiguationData":[OSD([subQ6])]})])],"derivedFrom":makeQuery(id+"F1.opExtrude","CAP_FACE",FACE,{"disambiguationData":[OSD([subQ6,subQ8,subQ9,subQ7,subQ4,subQ3,subQ2,subQ1,subQ0,subQ5,subQ10,subQ11])],"isStart":true})});}
            var sketch = newSketch(context, id + "F16", { "sketchPlane" : qUnion([Q0])});
            skLineSegment(sketch, "E79", {"start": v(0, 74.25) * mm, "end": v(0, 104.25) * mm, "construction": true});
            skCircle(sketch, "E80", {"center": v(0, 104.25) * mm, "radius": 6 * mm});
            skArc(sketch, "E81", {"start": v(15, 104.25) * mm, "mid": v(0, 119.25) * mm, "end": v(-15, 104.25) * mm});
            skLineSegment(sketch, "E82", {"start": v(15, 92.25) * mm, "end": v(33, 74.25) * mm});
            skLineSegment(sketch, "E83", {"start": v(15, 104.25) * mm, "end": v(15, 92.25) * mm});
            skLineSegment(sketch, "E84", {"start": v(-15, 92.25) * mm, "end": v(-15, 104.25) * mm});
            skLineSegment(sketch, "E85", {"start": v(-15, 92.25) * mm, "end": v(-33, 74.25) * mm});
            skLineSegment(sketch, "E86", {"start": v(-74.25, 0) * mm, "end": v(74.25, 0) * mm});
            skLineSegment(sketch, "E87.MirrorCS", {"start": v(15, -92.25) * mm, "end": v(33, -74.25) * mm});
            skLineSegment(sketch, "E88.MirrorCS", {"start": v(15, -104.25) * mm, "end": v(15, -92.25) * mm});
            skArc(sketch, "E89.MirrorCS", {"start": v(15, -104.25) * mm, "mid": v(0, -119.25) * mm, "end": v(-15, -104.25) * mm});
            skCircle(sketch, "E90.MirrorC", {"center": v(0, -104.25) * mm, "radius": 6 * mm});
            skLineSegment(sketch, "E91.MirrorCS", {"start": v(-15, -92.25) * mm, "end": v(-15, -104.25) * mm});
            skLineSegment(sketch, "E92.MirrorCS", {"start": v(-15, -92.25) * mm, "end": v(-33, -74.25) * mm});
            skLineSegment(sketch, "E93.MirrorCS", {"start": v(0, -74.25) * mm, "end": v(0, -104.25) * mm, "construction": true});
            skSolve(sketch);
        }
        {
            var Q0;
            {var subQ0=sQuery(id+"F16.wireOp",EDGE,"E87.MirrorCS");Q0=makeQuery(id+"F16.imprint","IMPRINT",FACE,{"disambiguationData":[TD([[makeQuery(id+"F16.imprint","IMPRINT",EDGE,{"derivedFrom":subQ0}),1.0]])]});}
            var Q1;
            Q1=makeQuery(id+"F16.imprint","IMPRINT",FACE,{"disambiguationData":[TD([[makeQuery(id+"F16.imprint","IMPRINT",EDGE,{"derivedFrom":makeQuery(id+"F1.opExtrude","CAP_EDGE",EDGE,{"disambiguationData":[OSD([sQuery(id+"F0.wireOp",EDGE,"E6")])],"isStart":true})}),-1.0]])]});
            var Q2;
            Q2=makeQuery(id+"F16.imprint","IMPRINT",FACE,{"disambiguationData":[TD([[makeQuery(id+"F16.imprint","IMPRINT",EDGE,{"derivedFrom":makeQuery(id+"F1.opExtrude","CAP_EDGE",EDGE,{"disambiguationData":[OSD([sQuery(id+"F0.wireOp",EDGE,"E4")])],"isStart":true})}),-1.0]])]});
            var Q3;
            Q3=makeQuery(id+"F16.imprint","IMPRINT",FACE,{"disambiguationData":[TD([[makeQuery(id+"F16.imprint","IMPRINT",EDGE,{"derivedFrom":sQuery(id+"F16.wireOp",EDGE,"E80")}),-1.0]])]});
            var Q4;
            Q4=makeQuery(id+"F2.opExtrude","CAP_FACE",FACE,{"disambiguationData":[OSD([sQuery(id+"F0.wireOp",EDGE,"E12"),sQuery(id+"F0.wireOp",EDGE,"E13"),sQuery(id+"F0.wireOp",EDGE,"E14"),sQuery(id+"F0.wireOp",EDGE,"E15"),sQuery(id+"F0.wireOp",EDGE,"E17.filletArc"),sQuery(id+"F0.wireOp",EDGE,"E18.filletArc"),sQuery(id+"F0.wireOp",EDGE,"E19.filletArc"),sQuery(id+"F0.wireOp",EDGE,"E20.filletArc"),sQuery(id+"F0.wireOp",EDGE,"E25.0"),sQuery(id+"F0.wireOp",EDGE,"E25.1"),sQuery(id+"F0.wireOp",EDGE,"E25.2"),sQuery(id+"F0.wireOp",EDGE,"E25.3"),sQuery(id+"F0.wireOp",EDGE,"E25.4"),sQuery(id+"F0.wireOp",EDGE,"E25.5"),sQuery(id+"F0.wireOp",EDGE,"E25.6"),sQuery(id+"F0.wireOp",EDGE,"E25.7")])],"isStart":false});
            extrude(context, id + "F17", {"entities" : qUnion([Q0, Q1, Q2, Q3]), "endBound" : BoundingType.UP_TO_SURFACE, "depth" : 25 * mm, "endBoundEntityFace" : qUnion([Q4]), "offsetDistance" : 25 * mm});
        }
    });
